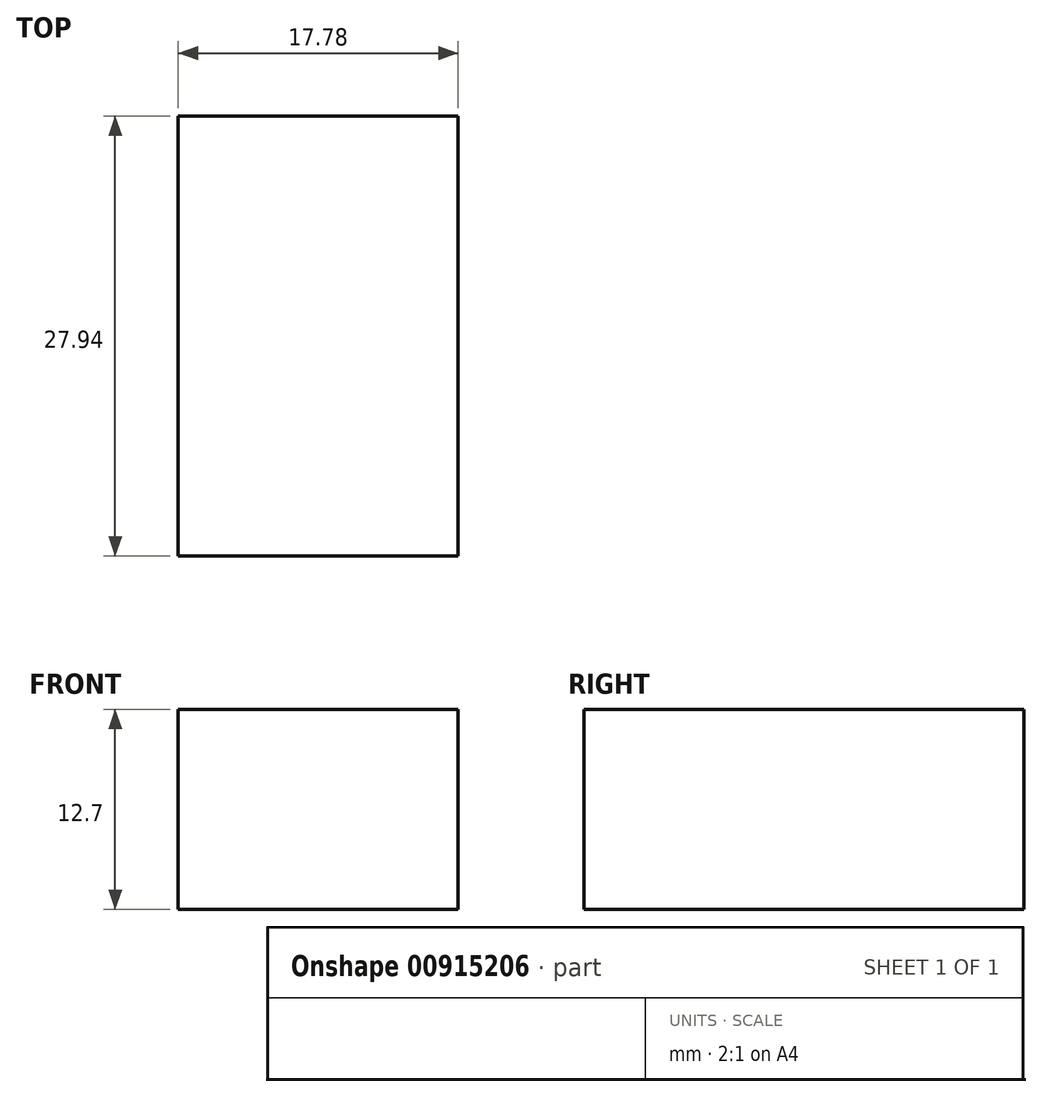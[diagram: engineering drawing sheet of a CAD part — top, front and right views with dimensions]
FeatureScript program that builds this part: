
annotation { "Feature Type Name" : "Feature", "Feature Type Description" : "" }
export const myFeature = defineFeature(function(context is Context, id is Id, definition is map)
    precondition{}
    {
        {
            var Q0;
            Q0=qCreatedBy(makeId("Front.planeOp"),FACE);
            var sketch = newSketch(context, id + "F0", { "sketchPlane" : qUnion([Q0])});
            skLineSegment(sketch, "E0.bottom", {"start": v(-8.87, 7.58) * mm, "end": v(8.9, 7.58) * mm});
            skLineSegment(sketch, "E0.top", {"start": v(-8.87, -5.12) * mm, "end": v(8.9, -5.12) * mm});
            skLineSegment(sketch, "E0.left", {"start": v(-8.87, 7.58) * mm, "end": v(-8.87, -5.12) * mm});
            skLineSegment(sketch, "E0.right", {"start": v(8.9, 7.58) * mm, "end": v(8.9, -5.12) * mm});
            skSolve(sketch);
        }
        {
            var Q0;
            Q0=makeQuery(id+"F0.imprint","IMPRINT",FACE,{"disambiguationData":[TD([[makeQuery(id+"F0.imprint","IMPRINT",EDGE,{"derivedFrom":sQuery(id+"F0.wireOp",EDGE,"E0.bottom")}),-1.0]])]});
            extrude(context, id + "F1", {"entities" : qUnion([Q0]), "depth" : 27.94 * mm, "offsetDistance" : 25.4 * mm});
        }
    });
